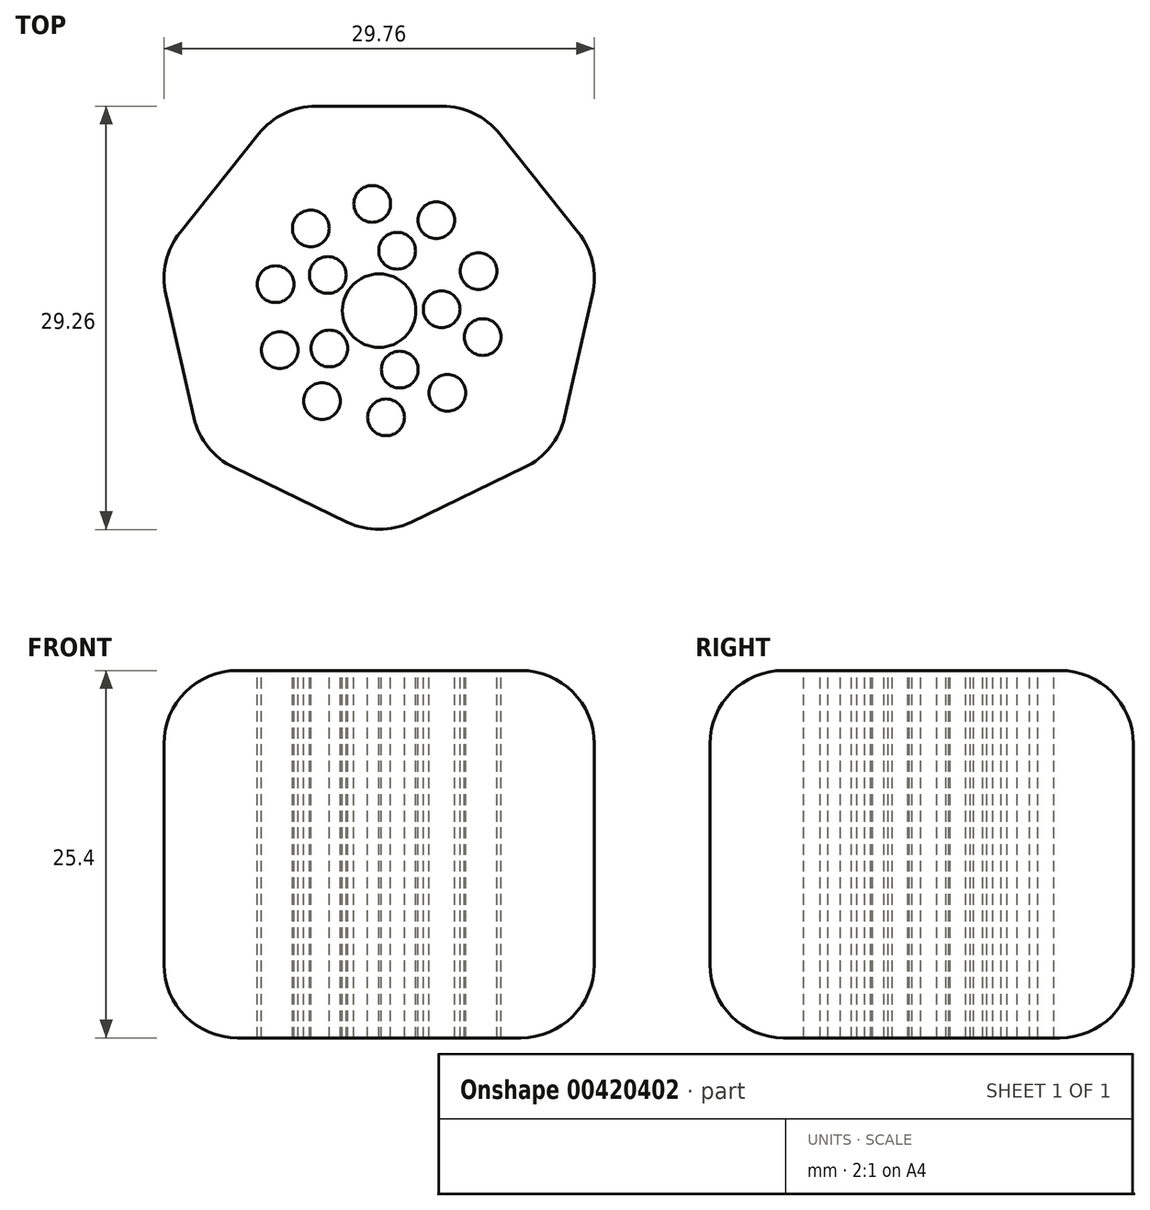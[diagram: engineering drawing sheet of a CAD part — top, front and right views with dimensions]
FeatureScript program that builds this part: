
annotation { "Feature Type Name" : "Feature", "Feature Type Description" : "" }
export const myFeature = defineFeature(function(context is Context, id is Id, definition is map)
    precondition{}
    {
        {
            var Q0;
            Q0=qCreatedBy(makeId("Top.planeOp"),FACE);
            var sketch = newSketch(context, id + "F0", { "sketchPlane" : qUnion([Q0])});
            skCircle(sketch, "E0.cCircle", {"center": v(0, 0) * mm, "radius": 14.13 * mm, "construction": true});
            skLineSegment(sketch, "E0.0", {"start": v(-6.8, 14.13) * mm, "end": v(6.8, 14.13) * mm});
            skLineSegment(sketch, "E0.1", {"start": v(6.8, 14.13) * mm, "end": v(15.3, 3.5) * mm});
            skLineSegment(sketch, "E0.2", {"start": v(15.3, 3.5) * mm, "end": v(12.26, -9.78) * mm});
            skLineSegment(sketch, "E0.3", {"start": v(12.26, -9.78) * mm, "end": v(0, -15.69) * mm});
            skLineSegment(sketch, "E0.4", {"start": v(0, -15.69) * mm, "end": v(-12.26, -9.78) * mm});
            skLineSegment(sketch, "E0.5", {"start": v(-12.26, -9.78) * mm, "end": v(-15.3, 3.5) * mm});
            skLineSegment(sketch, "E0.6", {"start": v(-15.3, 3.5) * mm, "end": v(-6.8, 14.13) * mm});
            skPoint(sketch, "E0.0.midPoint", {"position": v(0, 14.13) * mm});
            skSolve(sketch);
        }
        {
            var Q0;
            Q0=qSketchRegion(id+"F0",true);
            extrude(context, id + "F1", {"entities" : qUnion([Q0]), "depth" : 25.4 * mm});
        }
        {
            var Q0;
            Q0=makeQuery(id+"F1.opExtrude","SWEPT_EDGE",EDGE,{"disambiguationData":[OSD([sQuery(id+"F0.wireOp",EDGE,"E0.4"),sQuery(id+"F0.wireOp",EDGE,"E0.5")])]});
            var Q1;
            Q1=makeQuery(id+"F1.opExtrude","SWEPT_EDGE",EDGE,{"disambiguationData":[OSD([sQuery(id+"F0.wireOp",EDGE,"E0.5"),sQuery(id+"F0.wireOp",EDGE,"E0.6")])]});
            var Q2;
            Q2=makeQuery(id+"F1.opExtrude","SWEPT_EDGE",EDGE,{"disambiguationData":[OSD([sQuery(id+"F0.wireOp",EDGE,"E0.0"),sQuery(id+"F0.wireOp",EDGE,"E0.6")])]});
            var Q3;
            Q3=makeQuery(id+"F1.opExtrude","SWEPT_EDGE",EDGE,{"disambiguationData":[OSD([sQuery(id+"F0.wireOp",EDGE,"E0.0"),sQuery(id+"F0.wireOp",EDGE,"E0.1")])]});
            var Q4;
            Q4=makeQuery(id+"F1.opExtrude","SWEPT_EDGE",EDGE,{"disambiguationData":[OSD([sQuery(id+"F0.wireOp",EDGE,"E0.1"),sQuery(id+"F0.wireOp",EDGE,"E0.2")])]});
            var Q5;
            Q5=makeQuery(id+"F1.opExtrude","SWEPT_EDGE",EDGE,{"disambiguationData":[OSD([sQuery(id+"F0.wireOp",EDGE,"E0.2"),sQuery(id+"F0.wireOp",EDGE,"E0.3")])]});
            var Q6;
            Q6=makeQuery(id+"F1.opExtrude","SWEPT_EDGE",EDGE,{"disambiguationData":[OSD([sQuery(id+"F0.wireOp",EDGE,"E0.3"),sQuery(id+"F0.wireOp",EDGE,"E0.4")])]});
            fillet(context, id + "F2", {"entities" : qUnion([Q0, Q1, Q2, Q3, Q4, Q5, Q6]), "radius" : 5.08 * mm, "tangentPropagation" : true, "allowEdgeOverflow" : false});
        }
        {
            var Q0;
            Q0=makeQuery(id+"F1.opExtrude","CAP_EDGE",EDGE,{"disambiguationData":[OSD([sQuery(id+"F0.wireOp",EDGE,"E0.0")])],"isStart":true});
            var Q1;
            Q1=makeQuery(id+"F1.opExtrude","CAP_FACE",FACE,{"disambiguationData":[OSD([sQuery(id+"F0.wireOp",EDGE,"E0.0"),sQuery(id+"F0.wireOp",EDGE,"E0.1"),sQuery(id+"F0.wireOp",EDGE,"E0.2"),sQuery(id+"F0.wireOp",EDGE,"E0.3"),sQuery(id+"F0.wireOp",EDGE,"E0.4"),sQuery(id+"F0.wireOp",EDGE,"E0.5"),sQuery(id+"F0.wireOp",EDGE,"E0.6")])],"isStart":false});
            fillet(context, id + "F3", {"entities" : qUnion([Q0, Q1]), "radius" : 5.08 * mm, "tangentPropagation" : true, "allowEdgeOverflow" : false});
        }
        {
            var Q0;
            Q0=makeQuery(id+"F1.opExtrude","CAP_FACE",FACE,{"disambiguationData":[OSD([sQuery(id+"F0.wireOp",EDGE,"E0.0"),sQuery(id+"F0.wireOp",EDGE,"E0.1"),sQuery(id+"F0.wireOp",EDGE,"E0.2"),sQuery(id+"F0.wireOp",EDGE,"E0.3"),sQuery(id+"F0.wireOp",EDGE,"E0.4"),sQuery(id+"F0.wireOp",EDGE,"E0.5"),sQuery(id+"F0.wireOp",EDGE,"E0.6")])],"isStart":false});
            var sketch = newSketch(context, id + "F4", { "sketchPlane" : qUnion([Q0])});
            skCircle(sketch, "E1", {"center": v(-4.72, 5.69) * mm, "radius": 1.27 * mm});
            skCircle(sketch, "E2.1.0", {"center": v(-7.17, 1.83) * mm, "radius": 1.27 * mm});
            skCircle(sketch, "E2.2.0", {"center": v(-6.87, -2.74) * mm, "radius": 1.27 * mm});
            skCircle(sketch, "E2.3.0", {"center": v(-3.95, -6.25) * mm, "radius": 1.27 * mm});
            skCircle(sketch, "E2.4.0", {"center": v(0.48, -7.38) * mm, "radius": 1.27 * mm});
            skCircle(sketch, "E2.5.0", {"center": v(4.72, -5.69) * mm, "radius": 1.27 * mm});
            skCircle(sketch, "E2.6.0", {"center": v(7.17, -1.83) * mm, "radius": 1.27 * mm});
            skCircle(sketch, "E2.7.0", {"center": v(6.87, 2.74) * mm, "radius": 1.27 * mm});
            skCircle(sketch, "E2.8.0", {"center": v(3.95, 6.25) * mm, "radius": 1.27 * mm});
            skCircle(sketch, "E2.9.0", {"center": v(-0.48, 7.38) * mm, "radius": 1.27 * mm});
            skPoint(sketch, "E2.center", {"position": v(0, 0) * mm});
            skCircle(sketch, "E3", {"center": v(-3.55, 2.46) * mm, "radius": 1.27 * mm});
            skCircle(sketch, "E4.1.0", {"center": v(-3.44, -2.62) * mm, "radius": 1.27 * mm});
            skCircle(sketch, "E4.2.0", {"center": v(1.42, -4.08) * mm, "radius": 1.27 * mm});
            skCircle(sketch, "E4.3.0", {"center": v(4.32, 0.1) * mm, "radius": 1.27 * mm});
            skCircle(sketch, "E4.4.0", {"center": v(1.24, 4.14) * mm, "radius": 1.27 * mm});
            skCircle(sketch, "E5", {"center": v(0, 0) * mm, "radius": 2.54 * mm});
            skSolve(sketch);
        }
        {
            var Q0;
            Q0=makeQuery(id+"F4.imprint","IMPRINT",FACE,{"disambiguationData":[TD([[makeQuery(id+"F4.imprint","IMPRINT",EDGE,{"derivedFrom":sQuery(id+"F4.wireOp",EDGE,"E2.4.0")}),1.0]])]});
            var Q1;
            Q1=makeQuery(id+"F4.imprint","IMPRINT",FACE,{"disambiguationData":[TD([[makeQuery(id+"F4.imprint","IMPRINT",EDGE,{"derivedFrom":sQuery(id+"F4.wireOp",EDGE,"E4.1.0")}),1.0]])]});
            var Q2;
            Q2=makeQuery(id+"F4.imprint","IMPRINT",FACE,{"disambiguationData":[TD([[makeQuery(id+"F4.imprint","IMPRINT",EDGE,{"derivedFrom":sQuery(id+"F4.wireOp",EDGE,"E2.5.0")}),1.0]])]});
            var Q3;
            Q3=makeQuery(id+"F4.imprint","IMPRINT",FACE,{"disambiguationData":[TD([[makeQuery(id+"F4.imprint","IMPRINT",EDGE,{"derivedFrom":sQuery(id+"F4.wireOp",EDGE,"E2.6.0")}),1.0]])]});
            var Q4;
            Q4=makeQuery(id+"F4.imprint","IMPRINT",FACE,{"disambiguationData":[TD([[makeQuery(id+"F4.imprint","IMPRINT",EDGE,{"derivedFrom":sQuery(id+"F4.wireOp",EDGE,"E4.3.0")}),1.0]])]});
            var Q5;
            Q5=makeQuery(id+"F4.imprint","IMPRINT",FACE,{"disambiguationData":[TD([[makeQuery(id+"F4.imprint","IMPRINT",EDGE,{"derivedFrom":sQuery(id+"F4.wireOp",EDGE,"E2.7.0")}),1.0]])]});
            var Q6;
            Q6=makeQuery(id+"F4.imprint","IMPRINT",FACE,{"disambiguationData":[TD([[makeQuery(id+"F4.imprint","IMPRINT",EDGE,{"derivedFrom":sQuery(id+"F4.wireOp",EDGE,"E2.8.0")}),1.0]])]});
            var Q7;
            Q7=makeQuery(id+"F4.imprint","IMPRINT",FACE,{"disambiguationData":[TD([[makeQuery(id+"F4.imprint","IMPRINT",EDGE,{"derivedFrom":sQuery(id+"F4.wireOp",EDGE,"E4.4.0")}),1.0]])]});
            var Q8;
            Q8=makeQuery(id+"F4.imprint","IMPRINT",FACE,{"disambiguationData":[TD([[makeQuery(id+"F4.imprint","IMPRINT",EDGE,{"derivedFrom":sQuery(id+"F4.wireOp",EDGE,"E5")}),1.0]])]});
            var Q9;
            Q9=makeQuery(id+"F4.imprint","IMPRINT",FACE,{"disambiguationData":[TD([[makeQuery(id+"F4.imprint","IMPRINT",EDGE,{"derivedFrom":sQuery(id+"F4.wireOp",EDGE,"E4.2.0")}),1.0]])]});
            var Q10;
            Q10=makeQuery(id+"F4.imprint","IMPRINT",FACE,{"disambiguationData":[TD([[makeQuery(id+"F4.imprint","IMPRINT",EDGE,{"derivedFrom":sQuery(id+"F4.wireOp",EDGE,"E2.3.0")}),1.0]])]});
            var Q11;
            Q11=makeQuery(id+"F4.imprint","IMPRINT",FACE,{"disambiguationData":[TD([[makeQuery(id+"F4.imprint","IMPRINT",EDGE,{"derivedFrom":sQuery(id+"F4.wireOp",EDGE,"E2.2.0")}),1.0]])]});
            var Q12;
            Q12=makeQuery(id+"F4.imprint","IMPRINT",FACE,{"disambiguationData":[TD([[makeQuery(id+"F4.imprint","IMPRINT",EDGE,{"derivedFrom":sQuery(id+"F4.wireOp",EDGE,"E2.1.0")}),1.0]])]});
            var Q13;
            Q13=makeQuery(id+"F4.imprint","IMPRINT",FACE,{"disambiguationData":[TD([[makeQuery(id+"F4.imprint","IMPRINT",EDGE,{"derivedFrom":sQuery(id+"F4.wireOp",EDGE,"E3")}),1.0]])]});
            var Q14;
            Q14=makeQuery(id+"F4.imprint","IMPRINT",FACE,{"disambiguationData":[TD([[makeQuery(id+"F4.imprint","IMPRINT",EDGE,{"derivedFrom":sQuery(id+"F4.wireOp",EDGE,"E1")}),1.0]])]});
            var Q15;
            Q15=makeQuery(id+"F4.imprint","IMPRINT",FACE,{"disambiguationData":[TD([[makeQuery(id+"F4.imprint","IMPRINT",EDGE,{"derivedFrom":sQuery(id+"F4.wireOp",EDGE,"E2.9.0")}),1.0]])]});
            var Q16;
            Q16=sQuery(id+"F4.wireOp",EDGE,"E2.5.0");
            var Q17;
            Q17=sQuery(id+"F4.wireOp",EDGE,"E2.6.0");
            var Q18;
            Q18=sQuery(id+"F4.wireOp",EDGE,"E4.2.0");
            var Q19;
            Q19=sQuery(id+"F4.wireOp",EDGE,"E2.4.0");
            var Q20;
            Q20=sQuery(id+"F4.wireOp",EDGE,"E2.3.0");
            var Q21;
            Q21=sQuery(id+"F4.wireOp",EDGE,"E2.2.0");
            var Q22;
            Q22=sQuery(id+"F4.wireOp",EDGE,"E2.1.0");
            var Q23;
            Q23=sQuery(id+"F4.wireOp",EDGE,"E4.1.0");
            var Q24;
            Q24=sQuery(id+"F4.wireOp",EDGE,"E5");
            var Q25;
            Q25=sQuery(id+"F4.wireOp",EDGE,"E4.3.0");
            var Q26;
            Q26=sQuery(id+"F4.wireOp",EDGE,"E2.7.0");
            var Q27;
            Q27=sQuery(id+"F4.wireOp",EDGE,"E2.8.0");
            var Q28;
            Q28=sQuery(id+"F4.wireOp",EDGE,"E4.4.0");
            var Q29;
            Q29=sQuery(id+"F4.wireOp",EDGE,"E2.9.0");
            var Q30;
            Q30=sQuery(id+"F4.wireOp",EDGE,"E3");
            var Q31;
            Q31=sQuery(id+"F4.wireOp",EDGE,"E1");
            extrude(context, id + "F5", {"entities" : qUnion([Q0, Q1, Q2, Q3, Q4, Q5, Q6, Q7, Q8, Q9, Q10, Q11, Q12, Q13, Q14, Q15]), "operationType" : NewBodyOperationType.REMOVE, "surfaceEntities" : qUnion([Q16, Q17, Q18, Q19, Q20, Q21, Q22, Q23, Q24, Q25, Q26, Q27, Q28, Q29, Q30, Q31]), "oppositeDirection" : true, "depth" : 37.08 * mm});
        }
    });
